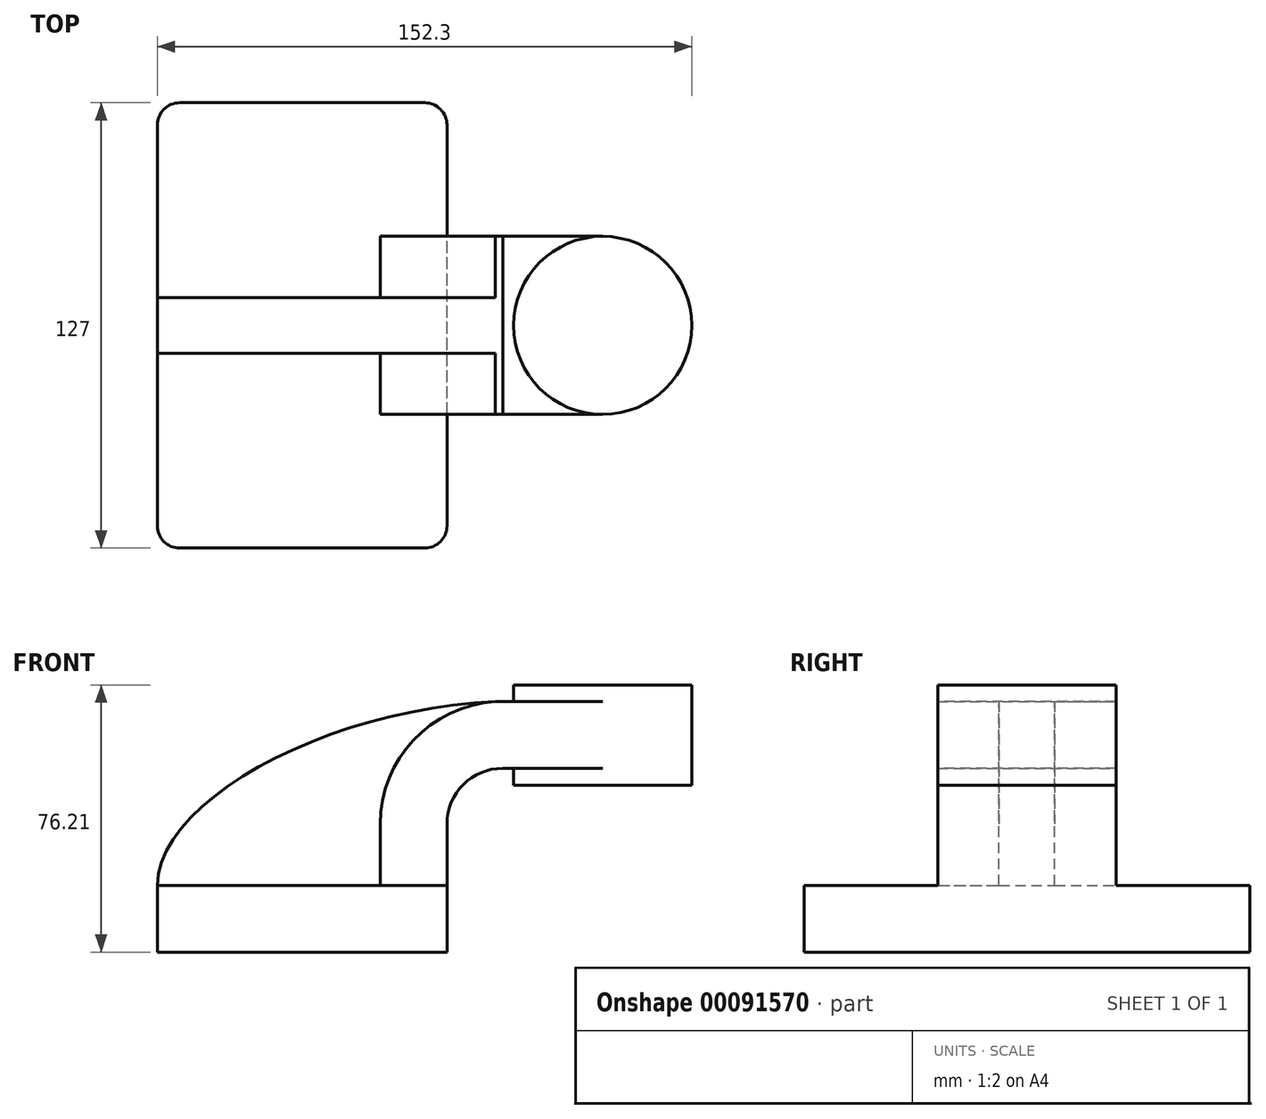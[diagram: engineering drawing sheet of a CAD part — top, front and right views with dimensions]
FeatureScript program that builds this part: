
annotation { "Feature Type Name" : "Feature", "Feature Type Description" : "" }
export const myFeature = defineFeature(function(context is Context, id is Id, definition is map)
    precondition{}
    {
        {
            var Q0;
            Q0=qCreatedBy(makeId("Front.planeOp"),FACE);
            var sketch = newSketch(context, id + "F0", { "sketchPlane" : qUnion([Q0])});
            skLineSegment(sketch, "E0.bottom", {"start": v(41.27, 9.53) * mm, "end": v(-41.28, 9.53) * mm});
            skLineSegment(sketch, "E0.top", {"start": v(41.28, -9.52) * mm, "end": v(-41.28, -9.52) * mm});
            skLineSegment(sketch, "E0.left", {"start": v(41.28, 9.53) * mm, "end": v(41.28, -9.52) * mm});
            skLineSegment(sketch, "E0.right", {"start": v(-41.28, 9.53) * mm, "end": v(-41.28, -9.52) * mm});
            skPoint(sketch, "E0.middle", {"position": v(0, 0) * mm});
            skLineSegment(sketch, "E1.bottom", {"start": v(60.22, 38.1) * mm, "end": v(111.02, 38.1) * mm});
            skLineSegment(sketch, "E1.top", {"start": v(60.22, 66.68) * mm, "end": v(111.02, 66.68) * mm});
            skLineSegment(sketch, "E1.left", {"start": v(60.22, 38.1) * mm, "end": v(60.22, 66.68) * mm});
            skLineSegment(sketch, "E1.right", {"start": v(111.02, 38.1) * mm, "end": v(111.02, 66.68) * mm});
            skPoint(sketch, "E1.middle", {"position": v(85.62, 52.39) * mm});
            skLineSegment(sketch, "E2", {"start": v(41.27, 9.53) * mm, "end": v(41.27, 27) * mm});
            skArc(sketch, "E3", {"start": v(41.27, 27) * mm, "mid": v(45.92, 38.23) * mm, "end": v(57.15, 42.88) * mm});
            skLineSegment(sketch, "E4", {"start": v(57.15, 42.88) * mm, "end": v(85.62, 42.88) * mm});
            skLineSegment(sketch, "E5.0", {"start": v(57.15, 61.93) * mm, "end": v(85.62, 61.93) * mm});
            skArc(sketch, "E5.1", {"start": v(22.22, 27) * mm, "mid": v(32.45, 51.7) * mm, "end": v(57.15, 61.93) * mm});
            skLineSegment(sketch, "E5.2", {"start": v(22.22, 9.53) * mm, "end": v(22.22, 27) * mm});
            skFitSpline(sketch, "E6", {"points": [v(-41.28, 9.53) * mm, v(57.15, 61.93) * mm], "startDerivative": vector(1.75, 76.98) * mm, "endDerivative": vector(139.41, 3.16) * mm});
            skLineSegment(sketch, "E7", {"start": v(85.62, 66.68) * mm, "end": v(85.62, 38.1) * mm});
            skPoint(sketch, "E8", {"position": v(85.62, 38.1) * mm});
            skSolve(sketch);
        }
        {
            var Q0;
            Q0=makeQuery(id+"F0.imprint","IMPRINT",FACE,{"disambiguationData":[TD([[makeQuery(id+"F0.imprint","IMPRINT",EDGE,{"derivedFrom":sQuery(id+"F0.wireOp",EDGE,"E0.top")}),-1.0]])]});
            extrude(context, id + "F1", {"entities" : qUnion([Q0]), "endBound" : BoundingType.SYMMETRIC, "depth" : 127 * mm});
        }
        {
            var Q0;
            {var subQ5=sQuery(id+"F0.wireOp",EDGE,"E2");Q0=makeQuery(id+"F0.imprint","IMPRINT",FACE,{"disambiguationData":[TD([[makeQuery(id+"F0.imprint","IMPRINT",EDGE,{"derivedFrom":subQ5}),1.0]])]});}
            var Q1;
            {var subQ0=sQuery(id+"F0.wireOp",EDGE,"E4");var subQ1=sQuery(id+"F0.wireOp",EDGE,"E1.left");var subQ2=makeQuery(id+"F0.imprint","INTERSECT",VERTEX,{"derivedFrom":[subQ1,subQ0]});Q1=makeQuery(id+"F0.imprint","IMPRINT",FACE,{"disambiguationData":[TD([[makeQuery(id+"F0.imprint","IMPRINT",EDGE,{"disambiguationData":[TD([[subQ2,-1.0]])],"derivedFrom":subQ1}),-1.0]])]});}
            extrude(context, id + "F2", {"entities" : qUnion([Q0, Q1]), "operationType" : NewBodyOperationType.ADD, "endBound" : BoundingType.SYMMETRIC, "depth" : 50.8 * mm});
        }
        {
            var Q0;
            {var subQ3=sQuery(id+"F0.wireOp",EDGE,"E5.2");Q0=makeQuery(id+"F0.imprint","IMPRINT",FACE,{"disambiguationData":[TD([[makeQuery(id+"F0.imprint","IMPRINT",EDGE,{"derivedFrom":subQ3}),1.0]])]});}
            extrude(context, id + "F3", {"entities" : qUnion([Q0]), "operationType" : NewBodyOperationType.ADD, "endBound" : BoundingType.SYMMETRIC, "depth" : 15.88 * mm});
        }
        {
            var Q0;
            {var subQ0=sQuery(id+"F0.wireOp",EDGE,"E1.right");Q0=makeQuery(id+"F0.imprint","IMPRINT",FACE,{"disambiguationData":[TD([[makeQuery(id+"F0.imprint","IMPRINT",EDGE,{"derivedFrom":subQ0}),1.0]])]});}
            var Q1;
            Q1=sQuery(id+"F0.wireOp",EDGE,"E7");
            revolve(context, id + "F4", {"operationType" : NewBodyOperationType.ADD, "entities" : qUnion([Q0]), "axis" : qUnion([Q1]), "revolveType" : RevolveType.FULL});
        }
        {
            var Q0;
            Q0=makeQuery(id+"F1.opExtrude","CAP_EDGE",EDGE,{"disambiguationData":[OSD([sQuery(id+"F0.wireOp",EDGE,"E0.left")])],"isStart":false});
            var Q1;
            Q1=makeQuery(id+"F1.opExtrude","CAP_EDGE",EDGE,{"disambiguationData":[OSD([sQuery(id+"F0.wireOp",EDGE,"E0.right")])],"isStart":false});
            var Q2;
            Q2=makeQuery(id+"F1.opExtrude","CAP_EDGE",EDGE,{"disambiguationData":[OSD([sQuery(id+"F0.wireOp",EDGE,"E0.left")])],"isStart":true});
            var Q3;
            Q3=makeQuery(id+"F1.opExtrude","CAP_EDGE",EDGE,{"disambiguationData":[OSD([sQuery(id+"F0.wireOp",EDGE,"E0.right")])],"isStart":true});
            fillet(context, id + "F5", {"entities" : qUnion([Q0, Q1, Q2, Q3]), "radius" : 6.35 * mm, "tangentPropagation" : true, "allowEdgeOverflow" : false});
        }
    });
